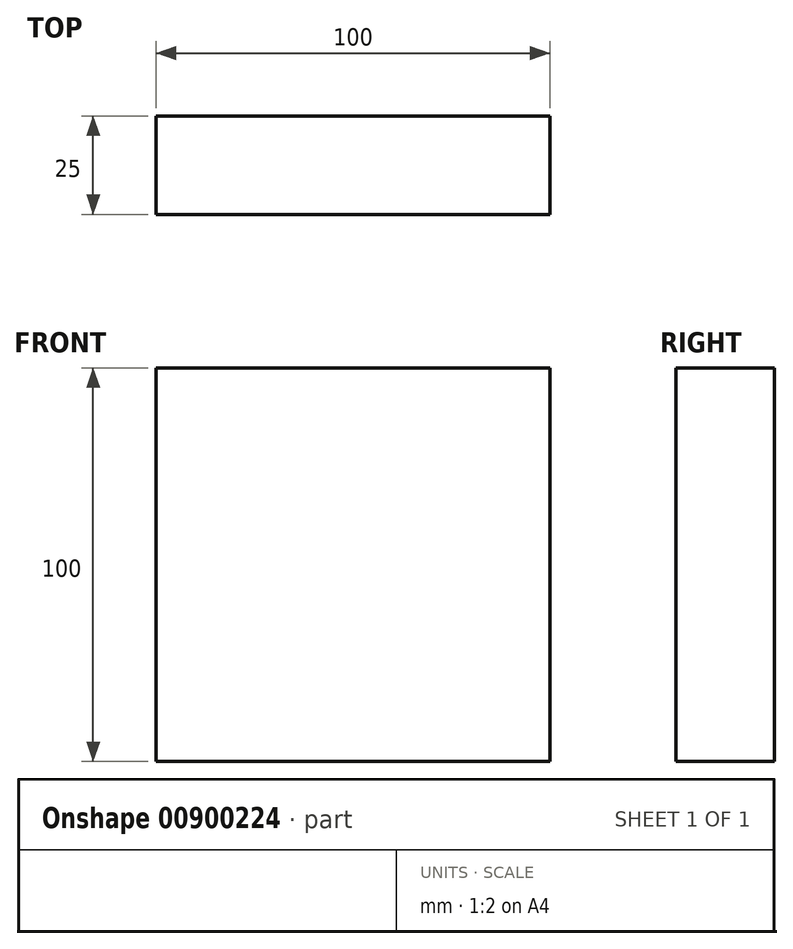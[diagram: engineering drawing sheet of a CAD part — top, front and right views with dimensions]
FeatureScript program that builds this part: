
annotation { "Feature Type Name" : "Feature", "Feature Type Description" : "" }
export const myFeature = defineFeature(function(context is Context, id is Id, definition is map)
    precondition{}
    {
        {
            var Q0;
            Q0=qCreatedBy(makeId("Front.planeOp"),FACE);
            var sketch = newSketch(context, id + "F0", { "sketchPlane" : qUnion([Q0])});
            skLineSegment(sketch, "E0.bottom", {"start": v(91.82, -230.46) * mm, "end": v(-8.18, -230.46) * mm});
            skLineSegment(sketch, "E0.top", {"start": v(91.82, -130.46) * mm, "end": v(-8.18, -130.46) * mm});
            skLineSegment(sketch, "E0.left", {"start": v(91.82, -230.46) * mm, "end": v(91.82, -130.46) * mm});
            skLineSegment(sketch, "E0.right", {"start": v(-8.18, -230.46) * mm, "end": v(-8.18, -130.46) * mm});
            skSolve(sketch);
        }
        {
            var Q0;
            Q0 = qSketchRegion(id + "F0", true);
            extrude(context, id + "F1", {"entities" : qUnion([Q0]), "depth" : 25 * mm, "offsetDistance" : 25 * mm});
        }
    });
